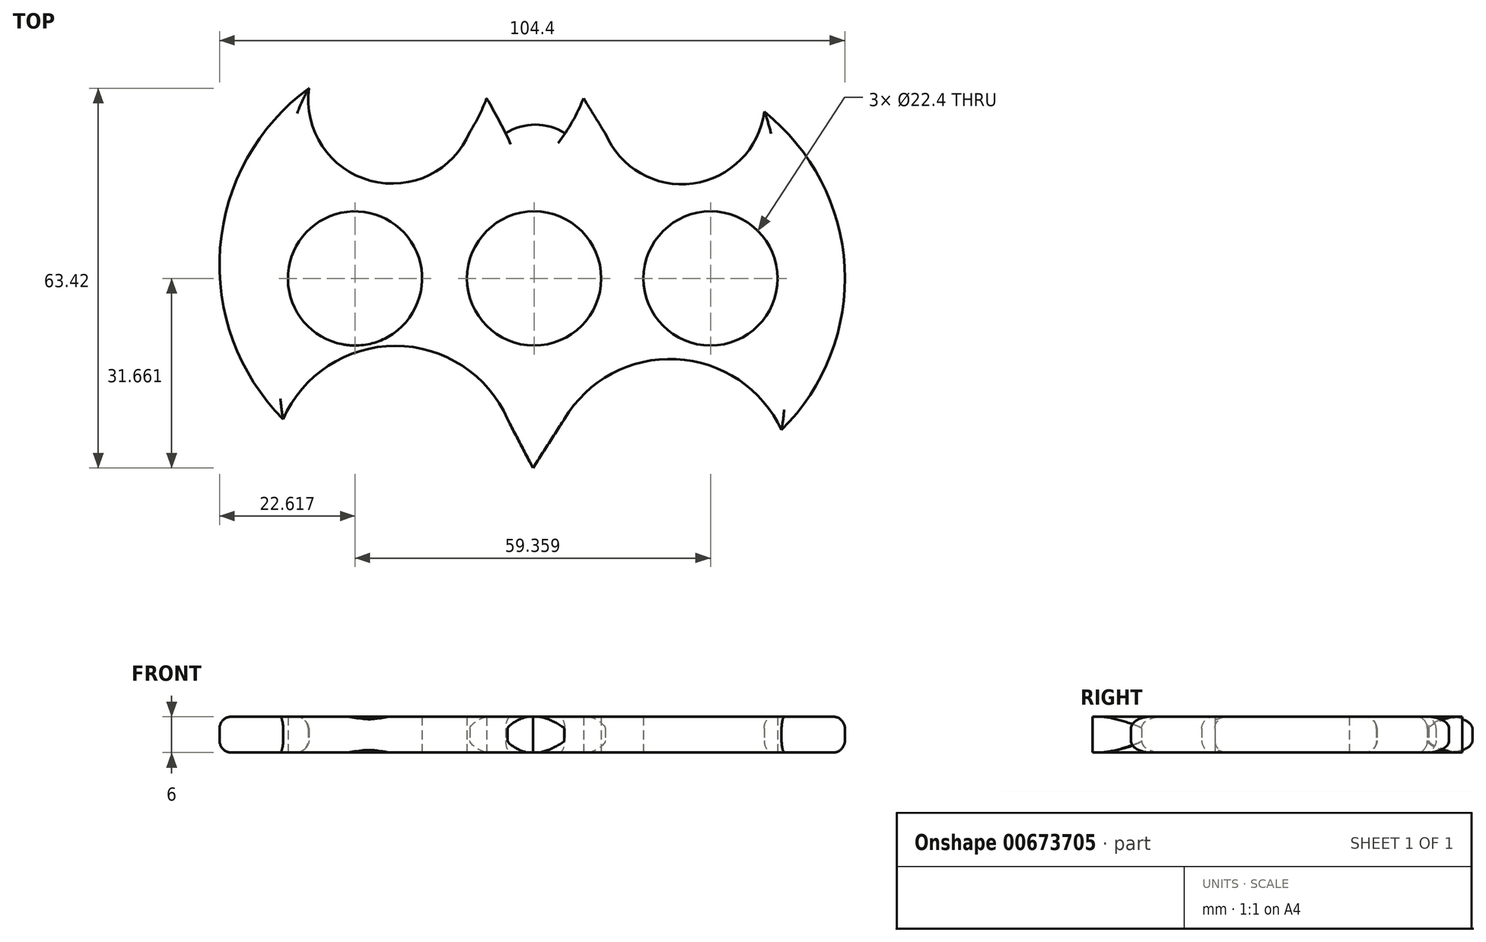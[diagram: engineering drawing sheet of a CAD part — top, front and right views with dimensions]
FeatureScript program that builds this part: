
annotation { "Feature Type Name" : "Feature", "Feature Type Description" : "" }
export const myFeature = defineFeature(function(context is Context, id is Id, definition is map)
    precondition{}
    {
        {
            var Q0;
            Q0=qCreatedBy(makeId("Top.planeOp"),FACE);
            var sketch = newSketch(context, id + "F0", { "sketchPlane" : qUnion([Q0])});
            skCircle(sketch, "E0", {"center": v(-0.82, 1.65) * mm, "radius": 11.2 * mm});
            skCircle(sketch, "E1", {"center": v(28.64, 1.65) * mm, "radius": 11.2 * mm});
            skCircle(sketch, "E2", {"center": v(-30.72, 1.65) * mm, "radius": 11.2 * mm});
            skArc(sketch, "E3", {"start": v(4.36, 25.87) * mm, "mid": v(-0.61, 27.33) * mm, "end": v(-5.59, 25.88) * mm});
            skArc(sketch, "E4", {"start": v(-5.59, 25.88) * mm, "mid": v(-7.11, 28.83) * mm, "end": v(-8.74, 31.72) * mm});
            skArc(sketch, "E5", {"start": v(4.36, 25.87) * mm, "mid": v(6.05, 28.71) * mm, "end": v(7.42, 31.72) * mm});
            skArc(sketch, "E6", {"start": v(-11.52, 26.13) * mm, "mid": v(-10, 28.86) * mm, "end": v(-8.74, 31.72) * mm});
            skPoint(sketch, "E7.end.orphan", {"position": v(6.75, -24.7) * mm});
            skArc(sketch, "E8", {"start": v(-5.26, -21.86) * mm, "mid": v(-24, -9.6) * mm, "end": v(-42.72, -21.86) * mm});
            skArc(sketch, "E9", {"start": v(40.5, -23.63) * mm, "mid": v(22.89, -11.82) * mm, "end": v(4.21, -21.86) * mm});
            skArc(sketch, "E10", {"start": v(-38.42, 33.4) * mm, "mid": v(-28.17, 17.97) * mm, "end": v(-11.52, 26.13) * mm});
            skArc(sketch, "E11", {"start": v(-38.42, 33.4) * mm, "mid": v(-53.23, 6.76) * mm, "end": v(-42.72, -21.86) * mm});
            skArc(sketch, "E12", {"start": v(11.05, 25.87) * mm, "mid": v(25.7, 17.5) * mm, "end": v(37.58, 29.49) * mm});
            skArc(sketch, "E13", {"start": v(40.5, -23.63) * mm, "mid": v(51, 3.58) * mm, "end": v(37.58, 29.49) * mm});
            skLineSegment(sketch, "E14", {"start": v(7.42, 31.72) * mm, "end": v(11.05, 25.87) * mm});
            skLineSegment(sketch, "E15", {"start": v(-5.26, -21.86) * mm, "end": v(-1.02, -30) * mm});
            skLineSegment(sketch, "E16", {"start": v(-1.02, -30) * mm, "end": v(4.21, -21.86) * mm});
            skSolve(sketch);
        }
        {
            var Q0;
            Q0=makeQuery(id+"F0.imprint","IMPRINT",FACE,{"disambiguationData":[TD([[makeQuery(id+"F0.imprint","IMPRINT",EDGE,{"derivedFrom":sQuery(id+"F0.wireOp",EDGE,"E0")}),-1.0]])]});
            extrude(context, id + "F1", {"entities" : qUnion([Q0]), "depth" : 6 * mm, "offsetDistance" : 25 * mm});
        }
        {
            var Q0;
            Q0=makeQuery(id+"F1.opExtrude","CAP_EDGE",EDGE,{"disambiguationData":[OSD([sQuery(id+"F0.wireOp",EDGE,"E10")])],"isStart":false});
            var Q1;
            Q1=makeQuery(id+"F1.opExtrude","CAP_EDGE",EDGE,{"disambiguationData":[OSD([sQuery(id+"F0.wireOp",EDGE,"E10")])],"isStart":true});
            var Q2;
            Q2=makeQuery(id+"F1.opExtrude","CAP_EDGE",EDGE,{"disambiguationData":[OSD([sQuery(id+"F0.wireOp",EDGE,"E3")])],"isStart":false});
            var Q3;
            Q3=makeQuery(id+"F1.opExtrude","CAP_EDGE",EDGE,{"disambiguationData":[OSD([sQuery(id+"F0.wireOp",EDGE,"E3")])],"isStart":true});
            var Q4;
            Q4=makeQuery(id+"F1.opExtrude","CAP_EDGE",EDGE,{"disambiguationData":[OSD([sQuery(id+"F0.wireOp",EDGE,"E11")])],"isStart":false});
            var Q5;
            Q5=makeQuery(id+"F1.opExtrude","CAP_EDGE",EDGE,{"disambiguationData":[OSD([sQuery(id+"F0.wireOp",EDGE,"E11")])],"isStart":true});
            var Q6;
            Q6=makeQuery(id+"F1.opExtrude","CAP_EDGE",EDGE,{"disambiguationData":[OSD([sQuery(id+"F0.wireOp",EDGE,"E8")])],"isStart":true});
            var Q7;
            Q7=makeQuery(id+"F1.opExtrude","CAP_EDGE",EDGE,{"disambiguationData":[OSD([sQuery(id+"F0.wireOp",EDGE,"E8")])],"isStart":false});
            var Q8;
            Q8=makeQuery(id+"F1.opExtrude","CAP_EDGE",EDGE,{"disambiguationData":[OSD([sQuery(id+"F0.wireOp",EDGE,"E9")])],"isStart":false});
            var Q9;
            Q9=makeQuery(id+"F1.opExtrude","CAP_EDGE",EDGE,{"disambiguationData":[OSD([sQuery(id+"F0.wireOp",EDGE,"E9")])],"isStart":true});
            var Q10;
            Q10=makeQuery(id+"F1.opExtrude","CAP_EDGE",EDGE,{"disambiguationData":[OSD([sQuery(id+"F0.wireOp",EDGE,"E13")])],"isStart":true});
            var Q11;
            Q11=makeQuery(id+"F1.opExtrude","CAP_EDGE",EDGE,{"disambiguationData":[OSD([sQuery(id+"F0.wireOp",EDGE,"E13")])],"isStart":false});
            var Q12;
            Q12=makeQuery(id+"F1.opExtrude","CAP_EDGE",EDGE,{"disambiguationData":[OSD([sQuery(id+"F0.wireOp",EDGE,"E12")])],"isStart":false});
            var Q13;
            Q13=makeQuery(id+"F1.opExtrude","CAP_EDGE",EDGE,{"disambiguationData":[OSD([sQuery(id+"F0.wireOp",EDGE,"E12")])],"isStart":true});
            fillet(context, id + "F2", {"entities" : qUnion([Q0, Q1, Q2, Q3, Q4, Q5, Q6, Q7, Q8, Q9, Q10, Q11, Q12, Q13]), "radius" : 2 * mm, "tangentPropagation" : true, "allowEdgeOverflow" : false});
        }
    });
